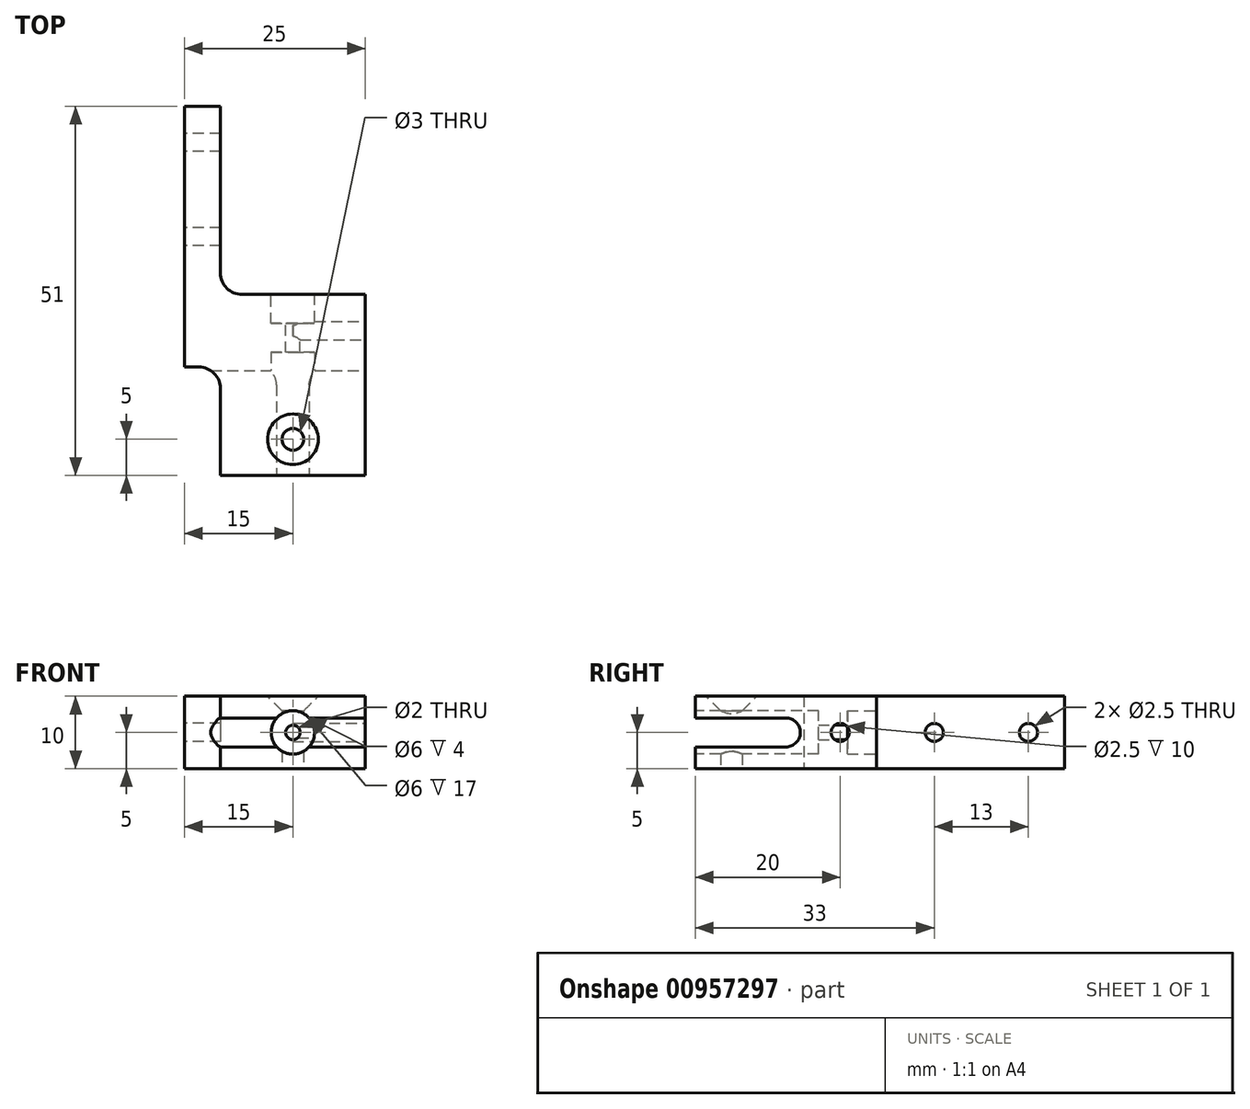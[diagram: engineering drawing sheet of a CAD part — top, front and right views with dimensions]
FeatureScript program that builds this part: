
annotation { "Feature Type Name" : "Feature", "Feature Type Description" : "" }
export const myFeature = defineFeature(function(context is Context, id is Id, definition is map)
    precondition{}
    {
        {
            var Q0;
            Q0=qCreatedBy(makeId("Top.planeOp"),FACE);
            var sketch = newSketch(context, id + "F0", { "sketchPlane" : qUnion([Q0])});
            skLineSegment(sketch, "E0", {"start": v(10, 0) * mm, "end": v(-10, 0) * mm});
            skLineSegment(sketch, "E1", {"start": v(-10, 0) * mm, "end": v(-10, 26) * mm});
            skLineSegment(sketch, "E2", {"start": v(-10, 26) * mm, "end": v(-15, 26) * mm});
            skLineSegment(sketch, "E3", {"start": v(-15, 26) * mm, "end": v(-15, -10) * mm});
            skLineSegment(sketch, "E4", {"start": v(-15, -10) * mm, "end": v(-10, -10) * mm});
            skLineSegment(sketch, "E5", {"start": v(-10, -10) * mm, "end": v(-10, -25) * mm});
            skLineSegment(sketch, "E6", {"start": v(-10, -25) * mm, "end": v(10, -25) * mm});
            skLineSegment(sketch, "E7", {"start": v(10, -25) * mm, "end": v(10, 0) * mm});
            skCircle(sketch, "E8", {"center": v(0, -20) * mm, "radius": 1.5 * mm});
            skArc(sketch, "E9", {"start": v(-10, 3) * mm, "mid": v(-9.12, 0.88) * mm, "end": v(-7, 0) * mm});
            skArc(sketch, "E10", {"start": v(-10, -13) * mm, "mid": v(-10.88, -10.88) * mm, "end": v(-13, -10) * mm});
            skSolve(sketch);
        }
        {
            var Q0;
            Q0=makeQuery(id+"F0.imprint","IMPRINT",FACE,{"disambiguationData":[TD([[makeQuery(id+"F0.imprint","IMPRINT",EDGE,{"derivedFrom":sQuery(id+"F0.wireOp",EDGE,"E0")}),1.0]])]});
            var Q1;
            {var subQ0=sQuery(id+"F0.wireOp",EDGE,"E4");Q1=makeQuery(id+"F0.imprint","IMPRINT",FACE,{"disambiguationData":[TD([[makeQuery(id+"F0.imprint","IMPRINT",EDGE,{"derivedFrom":subQ0}),-1.0]])]});}
            var Q2;
            {var subQ3=sQuery(id+"F0.wireOp",EDGE,"E9");Q2=makeQuery(id+"F0.imprint","IMPRINT",FACE,{"disambiguationData":[TD([[makeQuery(id+"F0.imprint","IMPRINT",EDGE,{"derivedFrom":subQ3}),-1.0]])]});}
            extrude(context, id + "F1", {"entities" : qUnion([Q0, Q1, Q2]), "depth" : 10 * mm, "offsetDistance" : 25 * mm});
        }
        {
            var Q0;
            Q0=makeQuery(id+"F1.opExtrude","SWEPT_FACE",FACE,{"disambiguationData":[OSD([sQuery(id+"F0.wireOp",EDGE,"E7")])]});
            var sketch = newSketch(context, id + "F2", { "sketchPlane" : qUnion([Q0])});
            skLineSegment(sketch, "E11", {"start": v(-25, 7) * mm, "end": v(-25, 3) * mm});
            skLineSegment(sketch, "E12", {"start": v(-25, 7) * mm, "end": v(-12.5, 7) * mm});
            skPoint(sketch, "E12.endSnap0", {"position": v(-12.5, 0) * mm});
            skLineSegment(sketch, "E13", {"start": v(-25, 3) * mm, "end": v(-12.5, 3) * mm});
            skArc(sketch, "E14", {"start": v(-12.5, 7) * mm, "mid": v(-10.5, 5) * mm, "end": v(-12.5, 3) * mm});
            skCircle(sketch, "E15", {"center": v(-5, 5) * mm, "radius": 1.25 * mm});
            skSolve(sketch);
        }
        {
            var Q0;
            Q0=makeQuery(id+"F2.imprint","IMPRINT",FACE,{"disambiguationData":[TD([[makeQuery(id+"F2.imprint","IMPRINT",EDGE,{"derivedFrom":sQuery(id+"F2.wireOp",EDGE,"E11")}),1.0]])]});
            extrude(context, id + "F3", {"entities" : qUnion([Q0]), "operationType" : NewBodyOperationType.REMOVE, "endBound" : BoundingType.THROUGH_ALL, "oppositeDirection" : true, "depth" : 25 * mm, "offsetDistance" : 25 * mm});
        }
        {
            var Q0;
            Q0=makeQuery(id+"F1.opExtrude","SWEPT_FACE",FACE,{"disambiguationData":[OSD([sQuery(id+"F0.wireOp",EDGE,"E3")])]});
            var sketch = newSketch(context, id + "F4", { "sketchPlane" : qUnion([Q0])});
            skCircle(sketch, "E16", {"center": v(-8, 5) * mm, "radius": 1.25 * mm});
            skCircle(sketch, "E17", {"center": v(-21, 5) * mm, "radius": 1.25 * mm});
            skSolve(sketch);
        }
        {
            var Q0;
            Q0 = qSketchRegion(id + "F4", true);
            extrude(context, id + "F5", {"entities" : qUnion([Q0]), "operationType" : NewBodyOperationType.REMOVE, "endBound" : BoundingType.THROUGH_ALL, "oppositeDirection" : true, "depth" : 25 * mm, "offsetDistance" : 25 * mm});
        }
        {
            var Q0;
            Q0=makeQuery(id+"F1.opExtrude","SWEPT_FACE",FACE,{"disambiguationData":[OSD([sQuery(id+"F0.wireOp",EDGE,"E0")])]});
            var sketch = newSketch(context, id + "F6", { "sketchPlane" : qUnion([Q0])});
            skCircle(sketch, "E18", {"center": v(0, 5) * mm, "radius": 1 * mm});
            skCircle(sketch, "E19", {"center": v(0, 5) * mm, "radius": 3 * mm});
            skSolve(sketch);
        }
        {
            var Q0;
            Q0=makeQuery(id+"F6.imprint","IMPRINT",FACE,{"disambiguationData":[TD([[makeQuery(id+"F6.imprint","IMPRINT",EDGE,{"derivedFrom":sQuery(id+"F6.wireOp",EDGE,"E18")}),1.0]])]});
            extrude(context, id + "F7", {"entities" : qUnion([Q0]), "operationType" : NewBodyOperationType.REMOVE, "endBound" : BoundingType.THROUGH_ALL, "oppositeDirection" : true, "depth" : 25 * mm, "offsetDistance" : 25 * mm});
        }
        {
            var Q0;
            Q0 = qSketchRegion(id + "F6", true);
            extrude(context, id + "F8", {"entities" : qUnion([Q0]), "operationType" : NewBodyOperationType.REMOVE, "oppositeDirection" : true, "depth" : 4 * mm, "offsetDistance" : 25 * mm});
        }
        {
            var Q0;
            Q0=makeQuery(id+"F2.imprint","IMPRINT",FACE,{"disambiguationData":[TD([[makeQuery(id+"F2.imprint","IMPRINT",EDGE,{"derivedFrom":sQuery(id+"F2.wireOp",EDGE,"E15")}),1.0]])]});
            extrude(context, id + "F9", {"entities" : qUnion([Q0]), "operationType" : NewBodyOperationType.REMOVE, "oppositeDirection" : true, "depth" : 10 * mm, "offsetDistance" : 25 * mm});
        }
        {
            var Q0;
            Q0=makeQuery(id+"F1.opExtrude","CAP_EDGE",EDGE,{"disambiguationData":[OSD([sQuery(id+"F0.wireOp",EDGE,"E8")])],"isStart":false});
            var Q1;
            Q1=makeQuery(id+"F5.boolean.opBoolean","COPY",EDGE,{"derivedFrom":makeQuery(id+"F5.opExtrude","CAP_EDGE",EDGE,{"disambiguationData":[OSD([sQuery(id+"F4.wireOp",EDGE,"E17")])],"isStart":true})});
            chamfer(context, id + "F10", {"entities" : qUnion([Q0, Q1]), "width" : 2 * mm, "tangentPropagation" : true});
        }
        {
            var Q0;
            {var subQ1=sQuery(id+"F0.wireOp",EDGE,"E6");Q0=makeQuery(id+"F3.boolean.opBoolean","SPLIT",FACE,{"disambiguationData":[TD([makeQuery(id+"F3.opExtrude","SWEPT_FACE",FACE,{"disambiguationData":[OSD([sQuery(id+"F2.wireOp",EDGE,"E13")])]})])],"derivedFrom":makeQuery(id+"F1.opExtrude","SWEPT_FACE",FACE,{"disambiguationData":[OSD([subQ1])]})});}
            var sketch = newSketch(context, id + "F11", { "sketchPlane" : qUnion([Q0])});
            skCircle(sketch, "E20", {"center": v(0, 5) * mm, "radius": 3 * mm});
            skSolve(sketch);
        }
        {
            var Q0;
            Q0 = qSketchRegion(id + "F11", true);
            extrude(context, id + "F12", {"entities" : qUnion([Q0]), "operationType" : NewBodyOperationType.REMOVE, "oppositeDirection" : true, "depth" : 17 * mm, "offsetDistance" : 25 * mm});
        }
    });
